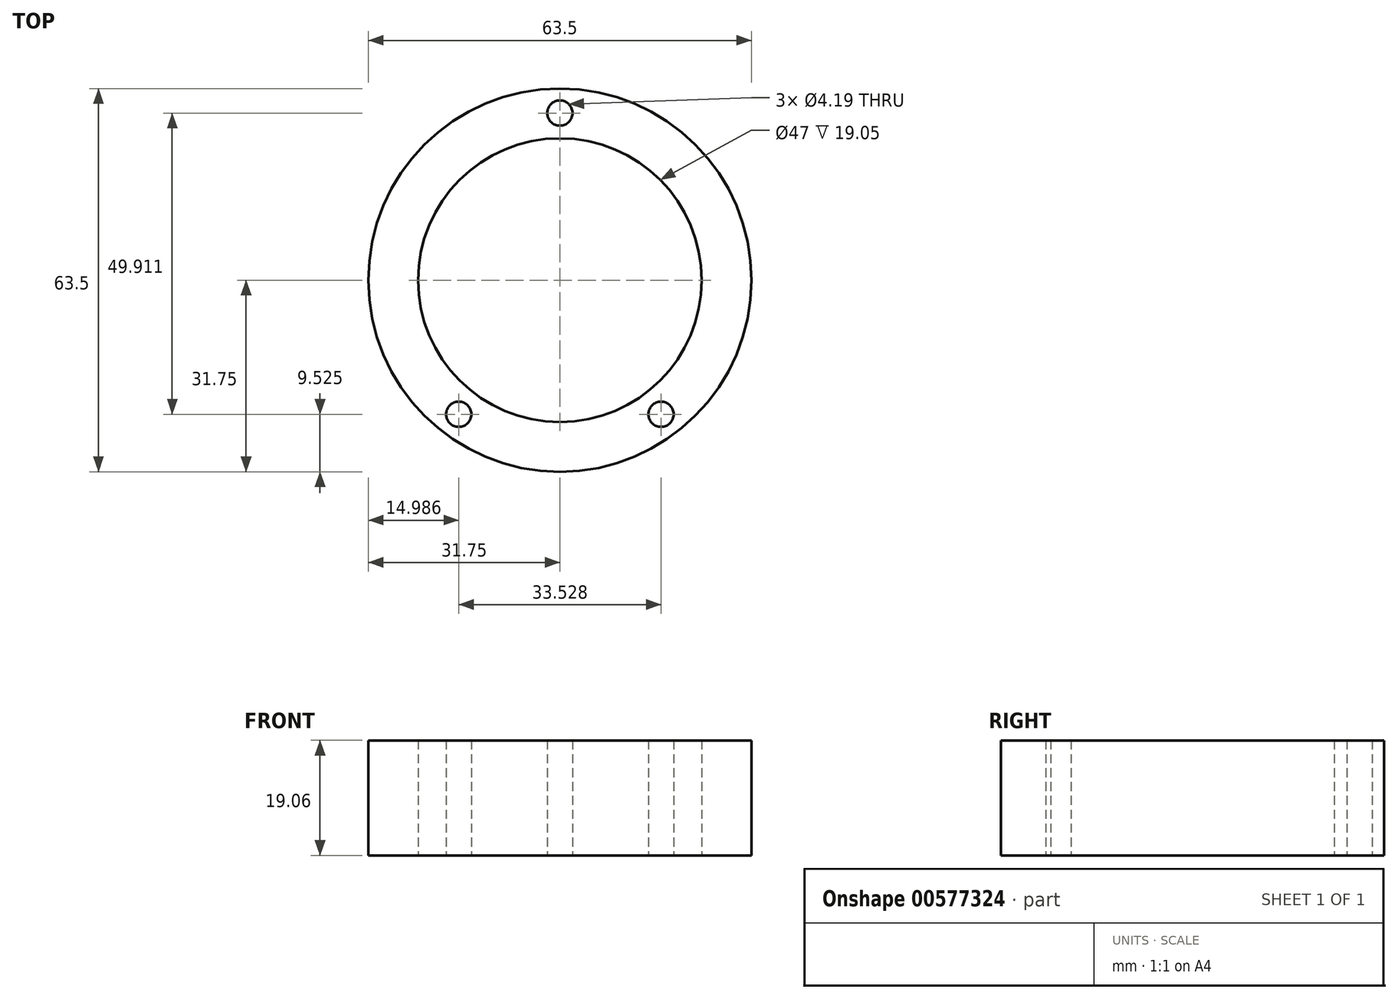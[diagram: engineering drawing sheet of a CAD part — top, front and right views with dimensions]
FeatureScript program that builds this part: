
annotation { "Feature Type Name" : "Feature", "Feature Type Description" : "" }
export const myFeature = defineFeature(function(context is Context, id is Id, definition is map)
    precondition{}
    {
        {
            var Q0;
            Q0=qCreatedBy(makeId("Top.planeOp"),FACE);
            var sketch = newSketch(context, id + "F0", { "sketchPlane" : qUnion([Q0])});
            skCircle(sketch, "E0", {"center": v(0, 0) * mm, "radius": 23.5 * mm});
            skCircle(sketch, "E1", {"center": v(0, 0) * mm, "radius": 31.75 * mm});
            skCircle(sketch, "E2", {"center": v(0, 27.69) * mm, "radius": 2.1 * mm});
            skCircle(sketch, "E3", {"center": v(16.76, -22.23) * mm, "radius": 2.1 * mm});
            skCircle(sketch, "E4", {"center": v(-16.76, -22.23) * mm, "radius": 2.1 * mm});
            skSolve(sketch);
        }
        {
            var Q0;
            Q0 = qSketchRegion(id + "F0", true);
            extrude(context, id + "F1", {"entities" : qUnion([Q0]), "endBound" : BoundingType.SYMMETRIC, "depth" : 19.05 * mm, "offsetDistance" : 25.4 * mm});
        }
    });
